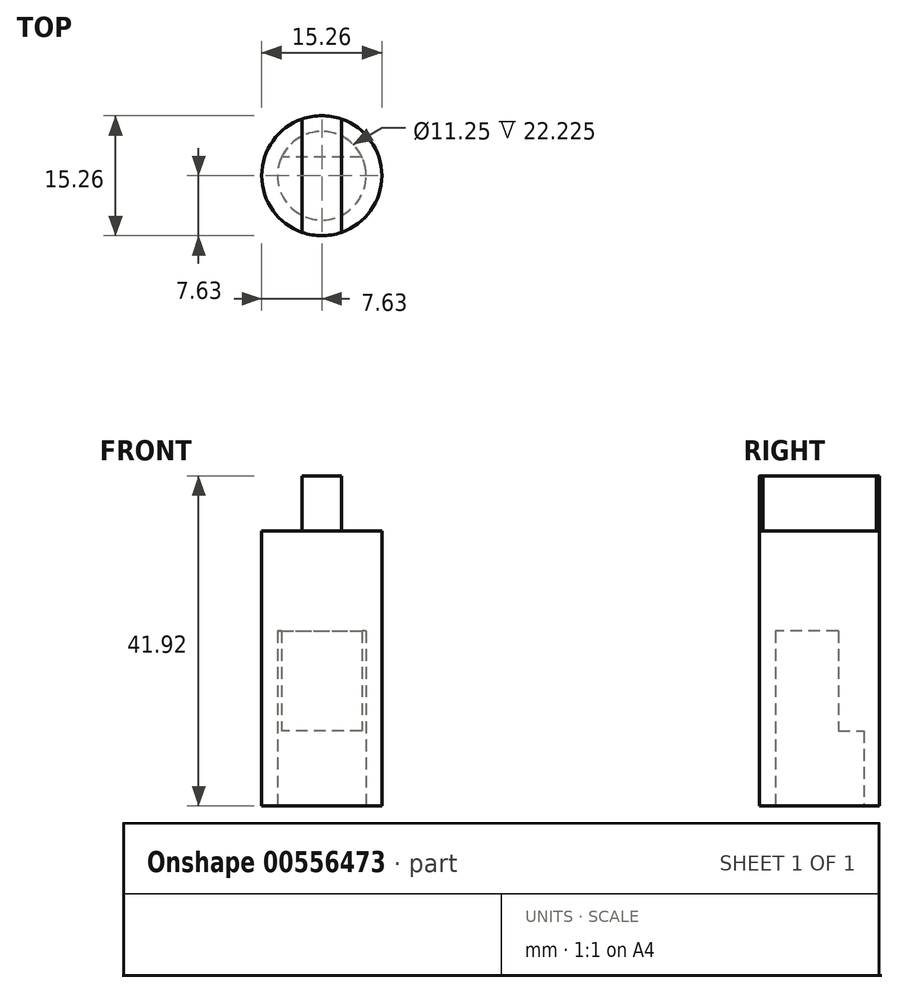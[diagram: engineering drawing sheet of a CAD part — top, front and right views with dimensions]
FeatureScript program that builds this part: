
annotation { "Feature Type Name" : "Feature", "Feature Type Description" : "" }
export const myFeature = defineFeature(function(context is Context, id is Id, definition is map)
    precondition{}
    {
        {
            var Q0;
            Q0=qCreatedBy(makeId("Top.planeOp"),FACE);
            var sketch = newSketch(context, id + "F0", { "sketchPlane" : qUnion([Q0])});
            skCircle(sketch, "E0", {"center": v(0, 0) * mm, "radius": 5.62 * mm});
            skCircle(sketch, "E1", {"center": v(0, 0) * mm, "radius": 7.62 * mm});
            skLineSegment(sketch, "E2", {"start": v(-5.1, 2.38) * mm, "end": v(5.1, 2.38) * mm});
            skSolve(sketch);
        }
        {
            var Q0;
            Q0=makeQuery(id+"F0.imprint","IMPRINT",FACE,{"disambiguationData":[TD([[makeQuery(id+"F0.imprint","IMPRINT",EDGE,{"derivedFrom":sQuery(id+"F0.wireOp",EDGE,"E1")}),1.0]])]});
            var Q1;
            {var subQ0=sQuery(id+"F0.wireOp",EDGE,"E2");Q1=makeQuery(id+"F0.imprint","IMPRINT",FACE,{"disambiguationData":[TD([[makeQuery(id+"F0.imprint","IMPRINT",EDGE,{"derivedFrom":subQ0}),-1.0]])]});}
            var Q2;
            {var subQ0=sQuery(id+"F0.wireOp",EDGE,"E2");Q2=makeQuery(id+"F0.imprint","IMPRINT",FACE,{"disambiguationData":[TD([[makeQuery(id+"F0.imprint","IMPRINT",EDGE,{"derivedFrom":subQ0}),1.0]])]});}
            extrude(context, id + "F1", {"entities" : qUnion([Q0, Q1, Q2]), "depth" : 34.92 * mm, "offsetDistance" : 25 * mm});
        }
        {
            var Q0;
            {var subQ0=sQuery(id+"F0.wireOp",EDGE,"E2");Q0=makeQuery(id+"F0.imprint","IMPRINT",FACE,{"disambiguationData":[TD([[makeQuery(id+"F0.imprint","IMPRINT",EDGE,{"derivedFrom":subQ0}),-1.0]])]});}
            var Q1;
            {var subQ0=sQuery(id+"F0.wireOp",EDGE,"E2");Q1=makeQuery(id+"F0.imprint","IMPRINT",FACE,{"disambiguationData":[TD([[makeQuery(id+"F0.imprint","IMPRINT",EDGE,{"derivedFrom":subQ0}),1.0]])]});}
            extrude(context, id + "F2", {"entities" : qUnion([Q0, Q1]), "operationType" : NewBodyOperationType.REMOVE, "depth" : 9.53 * mm, "offsetDistance" : 25 * mm});
        }
        {
            var Q0;
            {var subQ0=sQuery(id+"F0.wireOp",EDGE,"E2");Q0=makeQuery(id+"F0.imprint","IMPRINT",FACE,{"disambiguationData":[TD([[makeQuery(id+"F0.imprint","IMPRINT",EDGE,{"derivedFrom":subQ0}),-1.0]])]});}
            extrude(context, id + "F3", {"entities" : qUnion([Q0]), "operationType" : NewBodyOperationType.REMOVE, "depth" : 22.23 * mm, "offsetDistance" : 25 * mm});
        }
        {
            var Q0;
            Q0=makeQuery(id+"F1.opExtrude","CAP_FACE",FACE,{"disambiguationData":[OSD([sQuery(id+"F0.wireOp",EDGE,"E1")])],"isStart":false});
            var sketch = newSketch(context, id + "F4", { "sketchPlane" : qUnion([Q0])});
            skCircle(sketch, "E3.0", {"center": v(0, 0) * mm, "radius": 7.62 * mm});
            skLineSegment(sketch, "E4", {"start": v(0, 7.62) * mm, "end": v(0, -7.62) * mm, "construction": true});
            skLineSegment(sketch, "E5", {"start": v(2.5, 7.2) * mm, "end": v(2.5, -7.2) * mm});
            skLineSegment(sketch, "E6.MirrorCS", {"start": v(-2.5, 7.2) * mm, "end": v(-2.5, -7.2) * mm});
            skSolve(sketch);
        }
        {
            var Q0;
            {var subQ0=sQuery(id+"F4.wireOp",EDGE,"E5");Q0=makeQuery(id+"F4.imprint","IMPRINT",FACE,{"disambiguationData":[TD([[makeQuery(id+"F4.imprint","IMPRINT",EDGE,{"derivedFrom":subQ0}),-1.0]])]});}
            extrude(context, id + "F5", {"entities" : qUnion([Q0]), "depth" : 7 * mm, "offsetDistance" : 25 * mm});
        }
    });
